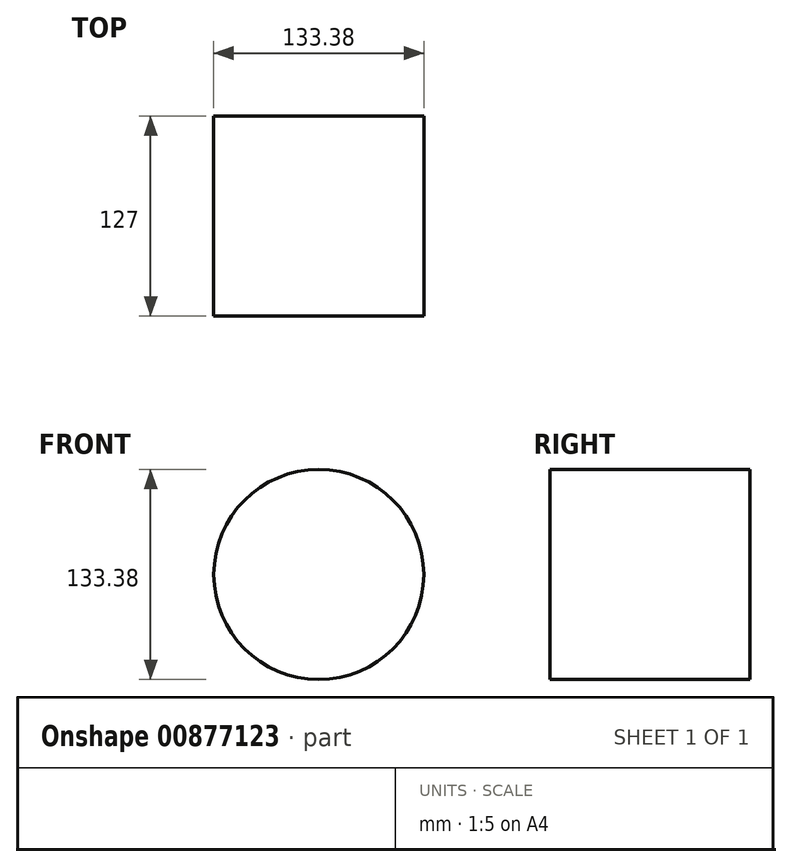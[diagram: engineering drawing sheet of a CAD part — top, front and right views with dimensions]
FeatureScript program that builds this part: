
annotation { "Feature Type Name" : "Feature", "Feature Type Description" : "" }
export const myFeature = defineFeature(function(context is Context, id is Id, definition is map)
    precondition{}
    {
        {
            var Q0;
            Q0=qCreatedBy(makeId("Front.planeOp"),FACE);
            var sketch = newSketch(context, id + "F0", { "sketchPlane" : qUnion([Q0])});
            skLineSegment(sketch, "E0.bottom", {"start": v(-63.5, 63.5) * mm, "end": v(63.5, 63.5) * mm});
            skLineSegment(sketch, "E0.top", {"start": v(-63.5, -63.5) * mm, "end": v(63.5, -63.5) * mm});
            skLineSegment(sketch, "E0.left", {"start": v(-63.5, 63.5) * mm, "end": v(-63.5, -63.5) * mm});
            skLineSegment(sketch, "E0.right", {"start": v(63.5, 63.5) * mm, "end": v(63.5, -63.5) * mm});
            skPoint(sketch, "E0.middle", {"position": v(0, 0) * mm});
            skSolve(sketch);
        }
        {
            var Q0;
            Q0=makeQuery(id+"F0.imprint","IMPRINT",FACE,{"disambiguationData":[TD([[makeQuery(id+"F0.imprint","IMPRINT",EDGE,{"derivedFrom":sQuery(id+"F0.wireOp",EDGE,"E0.bottom")}),-1.0]])]});
            var sketch = newSketch(context, id + "F1", { "sketchPlane" : qUnion([Q0])});
            skCircle(sketch, "E1", {"center": v(0, 0) * mm, "radius": 66.69 * mm});
            skSolve(sketch);
        }
        {
            var Q0;
            Q0 = qSketchRegion(id + "F1", true);
            extrude(context, id + "F2", {"entities" : qUnion([Q0]), "depth" : 127 * mm, "offsetDistance" : 25.4 * mm});
        }
    });
